# Revit family: Fireplace_Wood_HeatNGlo_Montana
name_source: partatom
category: Mechanical Equipment
revit_build: Autodesk Revit 2015 (Build: 20140323_1530(x64)
units: mm (PartAtom-declared; Revit-internal decimal feet)

## types (6) — shared parameters
Assembly Code = D3020
Construction Details = http://www.arcat.com
Default Elevation = 0' - 0"
Efficiency Ratings = as Specified
Fixture Finish = Metal - HeatNGlo - Metallic Black
Fuel Consumption = as Specified
HVAC_BTU Input = 0.0 Btu/h
HVAC_BTU Output = 0.0 Btu/h
Heating Capacity = as Specified
Keynote = 10305
Manufacturer = Heat & Glo
Manufacturer Website = http://www.heatnglo.com
Opening Height = 1' - 11 1/2"
Product Data = http://www.arcat.com
Revision = R2_2014-11
Sales Information = http://www.heatnglo.com
Send Message = http://www.arcat.com
Specification = http://www.arcat.com
Standards Conformance = as Specified
URL = http://www.heatnglo.com
Unit Depth = 1' - 11"
Unit Height = 3' - 6 3/8"
zero-valued in all types: Expected Lifespan (Years), Maintenance Schedule (Months), Warranty Duration (Years)

## per-type parameters (varying)
| type | Description | Fuel Type | Model | Opening Width | Rear Width | Unit Weight | Unit Width |
| 42x24 Viewing Area Gas Burning LP | Heat & Glo Gas Burning Outdoor Fireplace - MONTANA-42 as Specified | LP | MONTANA-42 | 3' - 6" | 2' - 7" | 250 | 4' - 0" |
| 42x24 Viewing Area Gas Burning NG | Heat & Glo Gas Burning Outdoor Fireplace - MONTANA-42 as Specified | NG | MONTANA-42 | 3' - 6" | 2' - 7" | 250 | 4' - 0" |
| 42x24 Viewing Area Wood Burning | Heat & Glo Woodburning Outdoor Fireplace - MONTANA-42 as Specified | Wood | MONTANA-42 | 3' - 6" | 2' - 7" | 250 | 4' - 0" |
| 36x24 Viewing Area Gas Burning LP | Heat & Glo Gas Burning Outdoor Fireplace - MONTANA-36 as Specified | LP | MONTANA-36 | 3' - 0" | 2' - 1" | 221 | 3' - 6" |
| 36x24 Viewing Area Gas Burning NG | Heat & Glo Gas Burning Outdoor Fireplace - MONTANA-36 as Specified | NG | MONTANA-36 | 3' - 0" | 2' - 1" | 221 | 3' - 6" |
| 36x24 Viewing Area Wood Burning | Heat & Glo Woodburning Outdoor Fireplace - MONTANA-36 as Specified | Wood | MONTANA-36 | 3' - 0" | 2' - 1" | 221 | 3' - 6" |

## geometry (parser evidence)
native form markers: Blend x10, Sweep x2
no freeform markers — native parametric forms only
